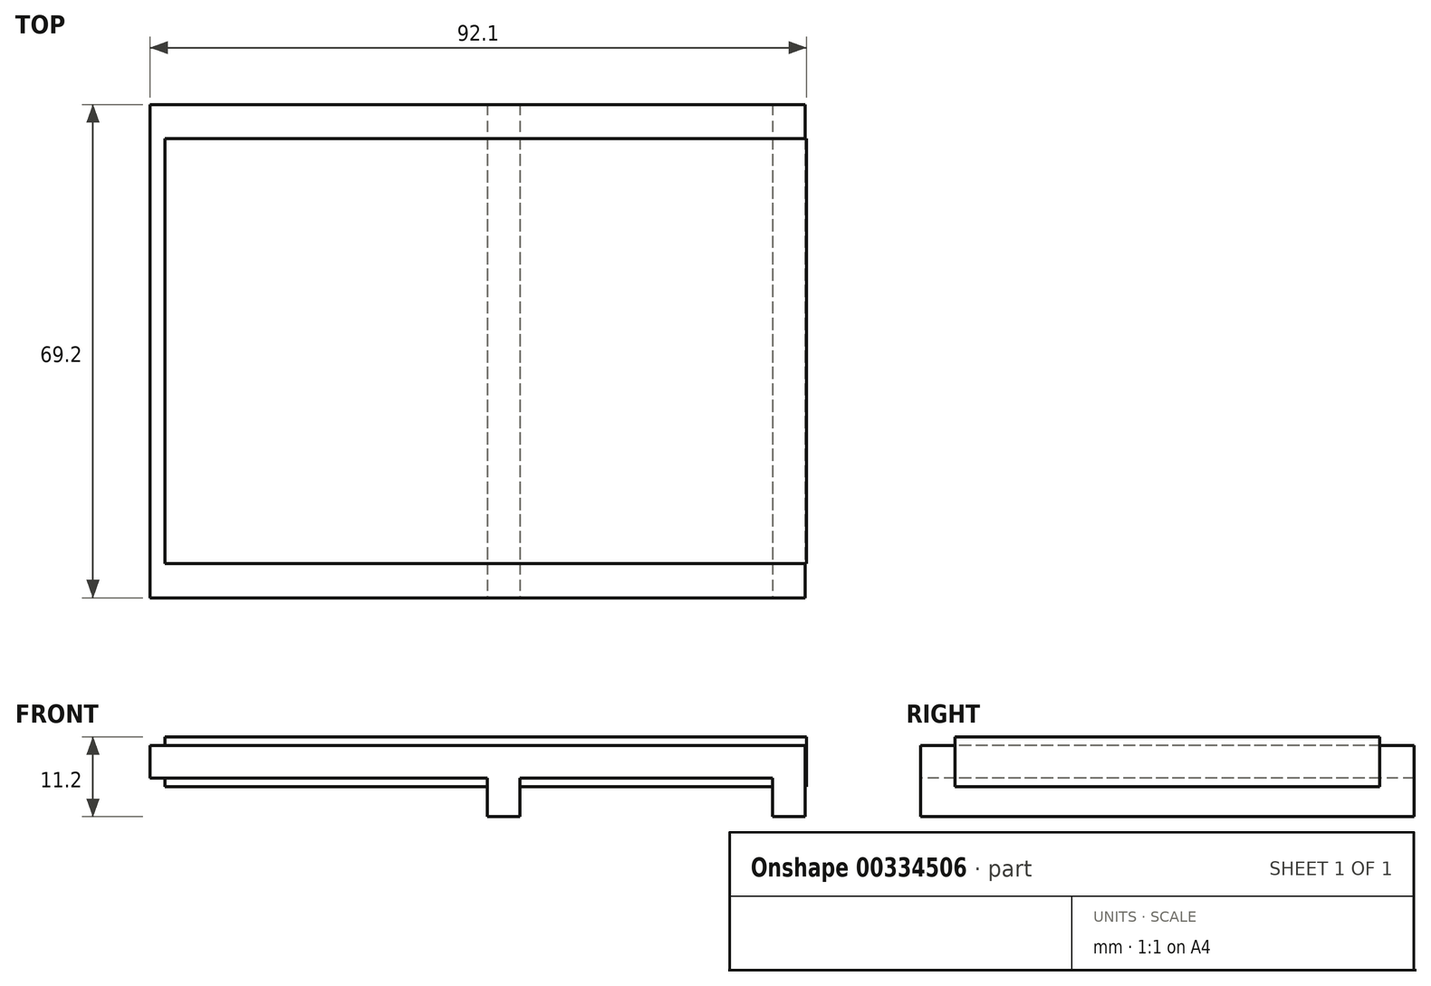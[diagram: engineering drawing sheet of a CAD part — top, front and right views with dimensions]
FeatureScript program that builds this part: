
annotation { "Feature Type Name" : "Feature", "Feature Type Description" : "" }
export const myFeature = defineFeature(function(context is Context, id is Id, definition is map)
    precondition{}
    {
        {
            var Q0;
            Q0=qCreatedBy(makeId("Top.planeOp"),FACE);
            var sketch = newSketch(context, id + "F0", { "sketchPlane" : qUnion([Q0])});
            skLineSegment(sketch, "E0.bottom", {"start": v(-27.73, 51.45) * mm, "end": v(64.17, 51.45) * mm});
            skLineSegment(sketch, "E0.top", {"start": v(-27.73, -17.75) * mm, "end": v(64.17, -17.75) * mm});
            skLineSegment(sketch, "E0.left", {"start": v(-27.73, 51.45) * mm, "end": v(-27.73, -17.75) * mm});
            skLineSegment(sketch, "E1.0", {"start": v(-25.63, 46.65) * mm, "end": v(-25.63, -12.95) * mm});
            skLineSegment(sketch, "E2.0", {"start": v(-25.63, 46.65) * mm, "end": v(64.37, 46.65) * mm});
            skLineSegment(sketch, "E3.0", {"start": v(-25.63, -12.95) * mm, "end": v(64.37, -12.95) * mm});
            skLineSegment(sketch, "E4.0", {"start": v(19.57, 51.45) * mm, "end": v(19.57, -17.75) * mm});
            skLineSegment(sketch, "E5.0", {"start": v(24.17, 51.45) * mm, "end": v(24.17, -17.75) * mm});
            skLineSegment(sketch, "E6", {"start": v(64.37, 46.65) * mm, "end": v(64.37, -12.95) * mm});
            skLineSegment(sketch, "E7.0", {"start": v(64.17, 46.65) * mm, "end": v(64.17, -12.95) * mm});
            skLineSegment(sketch, "E8", {"start": v(64.17, 46.65) * mm, "end": v(64.17, 51.45) * mm});
            skLineSegment(sketch, "E9", {"start": v(64.17, -12.95) * mm, "end": v(64.17, -17.75) * mm});
            skLineSegment(sketch, "E10.0", {"start": v(59.57, 46.65) * mm, "end": v(59.57, -12.95) * mm});
            skLineSegment(sketch, "E11", {"start": v(59.57, -12.95) * mm, "end": v(59.57, -17.75) * mm});
            skLineSegment(sketch, "E12", {"start": v(59.57, 46.65) * mm, "end": v(59.57, 51.45) * mm});
            skSolve(sketch);
        }
        {
            var Q0;
            {var subQ0=sQuery(id+"F0.wireOp",EDGE,"E0.left");Q0=makeQuery(id+"F0.imprint","IMPRINT",FACE,{"disambiguationData":[TD([[makeQuery(id+"F0.imprint","IMPRINT",EDGE,{"derivedFrom":subQ0}),1.0]])]});}
            var Q1;
            {var subQ0=sQuery(id+"F0.wireOp",EDGE,"E4.0");var subQ1=sQuery(id+"F0.wireOp",EDGE,"E0.bottom");var subQ2=makeQuery(id+"F0.imprint","INTERSECT",VERTEX,{"derivedFrom":[subQ1,subQ0]});Q1=makeQuery(id+"F0.imprint","IMPRINT",FACE,{"disambiguationData":[TD([[makeQuery(id+"F0.imprint","IMPRINT",EDGE,{"disambiguationData":[TD([[subQ2,-1.0]])],"derivedFrom":subQ1}),-1.0]])]});}
            var Q2;
            {var subQ3=sQuery(id+"F0.wireOp",EDGE,"E12");Q2=makeQuery(id+"F0.imprint","IMPRINT",FACE,{"disambiguationData":[TD([[makeQuery(id+"F0.imprint","IMPRINT",EDGE,{"derivedFrom":subQ3}),1.0]])]});}
            var Q3;
            {var subQ0=sQuery(id+"F0.wireOp",EDGE,"E8");Q3=makeQuery(id+"F0.imprint","IMPRINT",FACE,{"disambiguationData":[TD([[makeQuery(id+"F0.imprint","IMPRINT",EDGE,{"derivedFrom":subQ0}),1.0]])]});}
            var Q4;
            {var subQ0=sQuery(id+"F0.wireOp",EDGE,"E4.0");var subQ1=sQuery(id+"F0.wireOp",EDGE,"E0.top");var subQ2=makeQuery(id+"F0.imprint","INTERSECT",VERTEX,{"derivedFrom":[subQ1,subQ0]});Q4=makeQuery(id+"F0.imprint","IMPRINT",FACE,{"disambiguationData":[TD([[makeQuery(id+"F0.imprint","IMPRINT",EDGE,{"disambiguationData":[TD([[subQ2,-1.0]])],"derivedFrom":subQ1}),1.0]])]});}
            var Q5;
            {var subQ3=sQuery(id+"F0.wireOp",EDGE,"E11");Q5=makeQuery(id+"F0.imprint","IMPRINT",FACE,{"disambiguationData":[TD([[makeQuery(id+"F0.imprint","IMPRINT",EDGE,{"derivedFrom":subQ3}),-1.0]])]});}
            var Q6;
            {var subQ0=sQuery(id+"F0.wireOp",EDGE,"E9");Q6=makeQuery(id+"F0.imprint","IMPRINT",FACE,{"disambiguationData":[TD([[makeQuery(id+"F0.imprint","IMPRINT",EDGE,{"derivedFrom":subQ0}),-1.0]])]});}
            extrude(context, id + "F1", {"entities" : qUnion([Q0, Q1, Q2, Q3, Q4, Q5, Q6]), "endBound" : BoundingType.SYMMETRIC, "depth" : 4.6 * mm});
        }
        {
            var Q0;
            {var subQ0=sQuery(id+"F0.wireOp",EDGE,"E1.0");Q0=makeQuery(id+"F0.imprint","IMPRINT",FACE,{"disambiguationData":[TD([[makeQuery(id+"F0.imprint","IMPRINT",EDGE,{"derivedFrom":subQ0}),1.0]])]});}
            var Q1;
            {var subQ0=sQuery(id+"F0.wireOp",EDGE,"E4.0");var subQ1=sQuery(id+"F0.wireOp",EDGE,"E2.0");var subQ2=makeQuery(id+"F0.imprint","INTERSECT",VERTEX,{"derivedFrom":[subQ1,subQ0]});Q1=makeQuery(id+"F0.imprint","IMPRINT",FACE,{"disambiguationData":[TD([[makeQuery(id+"F0.imprint","IMPRINT",EDGE,{"disambiguationData":[TD([[subQ2,-1.0]])],"derivedFrom":subQ1}),-1.0]])]});}
            var Q2;
            {var subQ0=sQuery(id+"F0.wireOp",EDGE,"E10.0");Q2=makeQuery(id+"F0.imprint","IMPRINT",FACE,{"disambiguationData":[TD([[makeQuery(id+"F0.imprint","IMPRINT",EDGE,{"derivedFrom":subQ0}),-1.0]])]});}
            var Q3;
            {var subQ0=sQuery(id+"F0.wireOp",EDGE,"E7.0");Q3=makeQuery(id+"F0.imprint","IMPRINT",FACE,{"disambiguationData":[TD([[makeQuery(id+"F0.imprint","IMPRINT",EDGE,{"derivedFrom":subQ0}),-1.0]])]});}
            var Q4;
            {var subQ0=sQuery(id+"F0.wireOp",EDGE,"E6");Q4=makeQuery(id+"F0.imprint","IMPRINT",FACE,{"disambiguationData":[TD([[makeQuery(id+"F0.imprint","IMPRINT",EDGE,{"derivedFrom":subQ0}),-1.0]])]});}
            extrude(context, id + "F2", {"entities" : qUnion([Q0, Q1, Q2, Q3, Q4]), "operationType" : NewBodyOperationType.ADD, "endBound" : BoundingType.SYMMETRIC, "depth" : 7 * mm});
        }
        {
            var Q0;
            {var subQ0=sQuery(id+"F0.wireOp",EDGE,"E4.0");var subQ1=sQuery(id+"F0.wireOp",EDGE,"E2.0");var subQ2=makeQuery(id+"F0.imprint","INTERSECT",VERTEX,{"derivedFrom":[subQ1,subQ0]});Q0=makeQuery(id+"F0.imprint","IMPRINT",FACE,{"disambiguationData":[TD([[makeQuery(id+"F0.imprint","IMPRINT",EDGE,{"disambiguationData":[TD([[subQ2,-1.0]])],"derivedFrom":subQ1}),-1.0]])]});}
            var Q1;
            {var subQ0=sQuery(id+"F0.wireOp",EDGE,"E4.0");var subQ1=sQuery(id+"F0.wireOp",EDGE,"E0.bottom");var subQ2=makeQuery(id+"F0.imprint","INTERSECT",VERTEX,{"derivedFrom":[subQ1,subQ0]});Q1=makeQuery(id+"F0.imprint","IMPRINT",FACE,{"disambiguationData":[TD([[makeQuery(id+"F0.imprint","IMPRINT",EDGE,{"disambiguationData":[TD([[subQ2,-1.0]])],"derivedFrom":subQ1}),-1.0]])]});}
            var Q2;
            {var subQ0=sQuery(id+"F0.wireOp",EDGE,"E4.0");var subQ1=sQuery(id+"F0.wireOp",EDGE,"E0.top");var subQ2=makeQuery(id+"F0.imprint","INTERSECT",VERTEX,{"derivedFrom":[subQ1,subQ0]});Q2=makeQuery(id+"F0.imprint","IMPRINT",FACE,{"disambiguationData":[TD([[makeQuery(id+"F0.imprint","IMPRINT",EDGE,{"disambiguationData":[TD([[subQ2,-1.0]])],"derivedFrom":subQ1}),1.0]])]});}
            var Q3;
            {var subQ0=sQuery(id+"F0.wireOp",EDGE,"E9");Q3=makeQuery(id+"F0.imprint","IMPRINT",FACE,{"disambiguationData":[TD([[makeQuery(id+"F0.imprint","IMPRINT",EDGE,{"derivedFrom":subQ0}),-1.0]])]});}
            var Q4;
            {var subQ0=sQuery(id+"F0.wireOp",EDGE,"E7.0");Q4=makeQuery(id+"F0.imprint","IMPRINT",FACE,{"disambiguationData":[TD([[makeQuery(id+"F0.imprint","IMPRINT",EDGE,{"derivedFrom":subQ0}),-1.0]])]});}
            var Q5;
            {var subQ0=sQuery(id+"F0.wireOp",EDGE,"E8");Q5=makeQuery(id+"F0.imprint","IMPRINT",FACE,{"disambiguationData":[TD([[makeQuery(id+"F0.imprint","IMPRINT",EDGE,{"derivedFrom":subQ0}),1.0]])]});}
            extrude(context, id + "F3", {"entities" : qUnion([Q0, Q1, Q2, Q3, Q4, Q5]), "operationType" : NewBodyOperationType.ADD, "oppositeDirection" : true, "depth" : 7.7 * mm});
        }
    });
